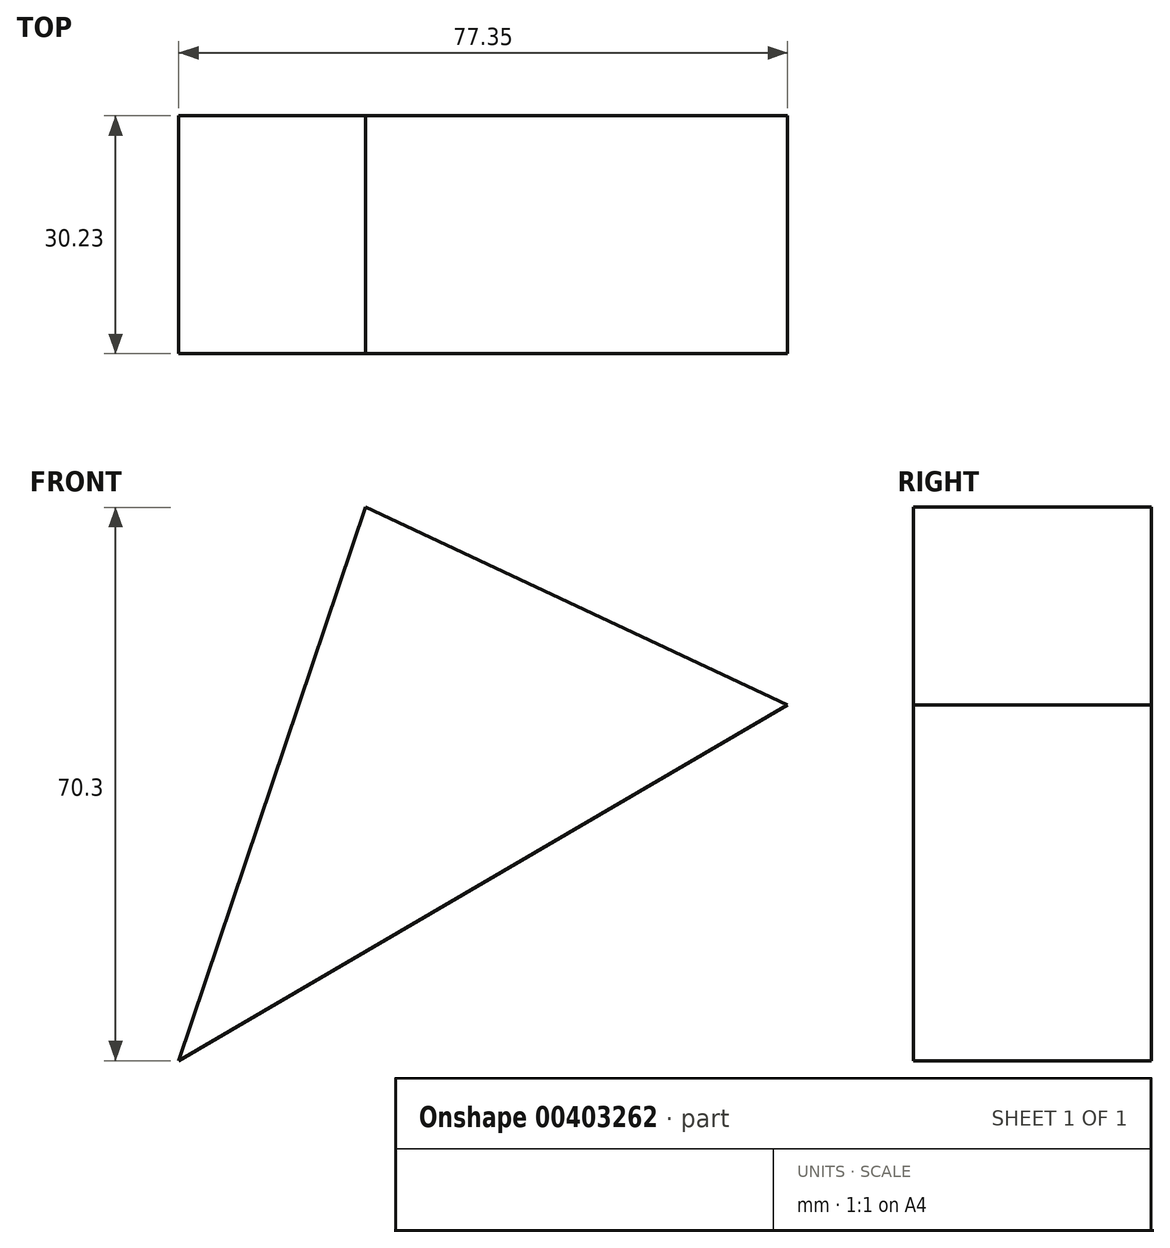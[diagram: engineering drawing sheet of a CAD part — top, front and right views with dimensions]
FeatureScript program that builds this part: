
annotation { "Feature Type Name" : "Feature", "Feature Type Description" : "" }
export const myFeature = defineFeature(function(context is Context, id is Id, definition is map)
    precondition{}
    {
        {
            var Q0;
            Q0=qCreatedBy(makeId("Front.planeOp"),FACE);
            var sketch = newSketch(context, id + "F0", { "sketchPlane" : qUnion([Q0])});
            skLineSegment(sketch, "E0", {"start": v(-20.86, 48.15) * mm, "end": v(-44.61, -22.15) * mm});
            skLineSegment(sketch, "E1", {"start": v(-44.61, -22.15) * mm, "end": v(32.74, 23.07) * mm});
            skLineSegment(sketch, "E2", {"start": v(32.74, 23.07) * mm, "end": v(-20.86, 48.15) * mm});
            skSolve(sketch);
        }
        {
            var Q0;
            Q0=makeQuery(id+"F0.imprint","IMPRINT",FACE,{"disambiguationData":[TD([[makeQuery(id+"F0.imprint","IMPRINT",EDGE,{"derivedFrom":sQuery(id+"F0.wireOp",EDGE,"E0")}),1.0]])]});
            extrude(context, id + "F1", {"entities" : qUnion([Q0]), "oppositeDirection" : true, "depth" : 30.23 * mm});
        }
    });
